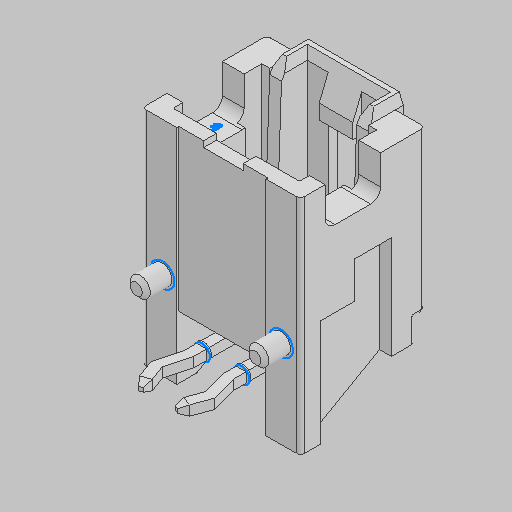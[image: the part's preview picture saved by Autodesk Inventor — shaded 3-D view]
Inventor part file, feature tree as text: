
AUTODESK INVENTOR PART (.ipt)
format: ipt  version: 2023.5 (Build 275446000, 446)  size: 271,360 bytes
history: native  units: in
note: dims shown in document units (in); Inventor stores cm internally (conversion verified against a paired STEP export)
features: other x1, extrude x1, sketch x1, imported_body x1
ambient origin geometry x8: Origin, YZ Plane, XZ Plane, XY Plane, X Axis, Y Axis, Z Axis, Center Point
bodies: Solid1 (feature_tree)
feature tree (4):
  other  "Repaired Geometry1"
  extrude  "Extrusion1"  Depth=0.0039in TaperAngle=0.0deg
  sketch  "3D Sketch1"
  imported_body  "Base1"
